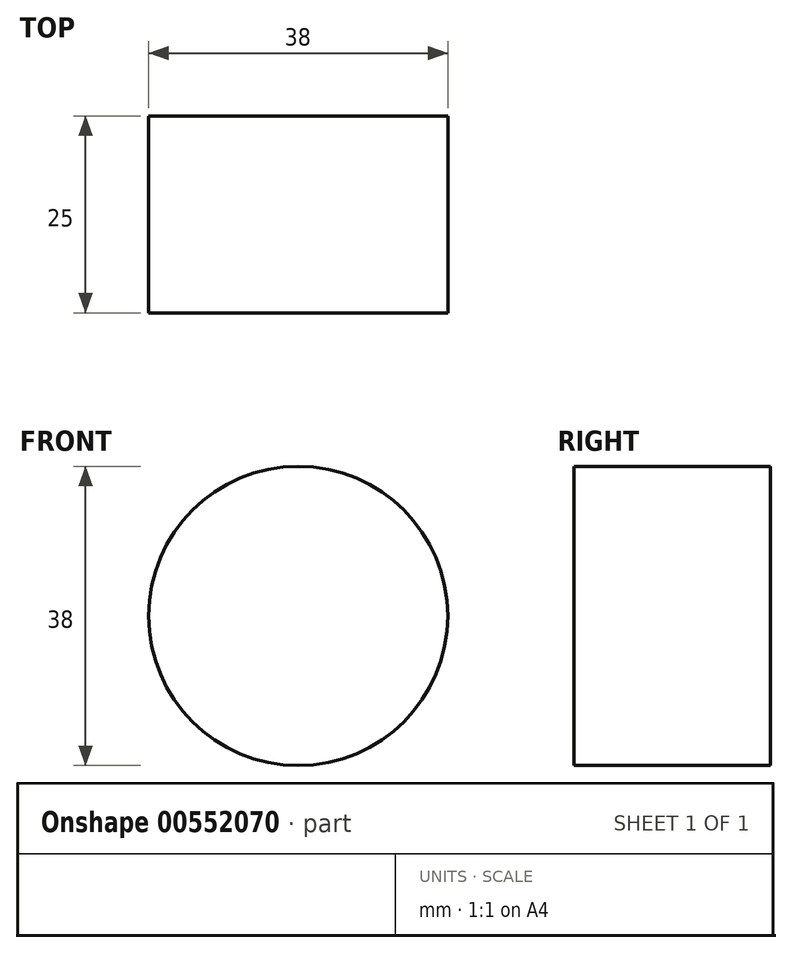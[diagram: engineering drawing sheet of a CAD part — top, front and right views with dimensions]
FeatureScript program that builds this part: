
annotation { "Feature Type Name" : "Feature", "Feature Type Description" : "" }
export const myFeature = defineFeature(function(context is Context, id is Id, definition is map)
    precondition{}
    {
        {
            var Q0;
            Q0=qCreatedBy(makeId("Front.planeOp"),FACE);
            var sketch = newSketch(context, id + "F0", { "sketchPlane" : qUnion([Q0])});
            skCircle(sketch, "E0", {"center": v(-46.93, 38.17) * mm, "radius": 19 * mm});
            skSolve(sketch);
        }
        {
            var Q0;
            Q0 = qSketchRegion(id + "F0", true);
            extrude(context, id + "F1", {"entities" : qUnion([Q0]), "depth" : 25 * mm, "offsetDistance" : 25 * mm});
        }
    });
